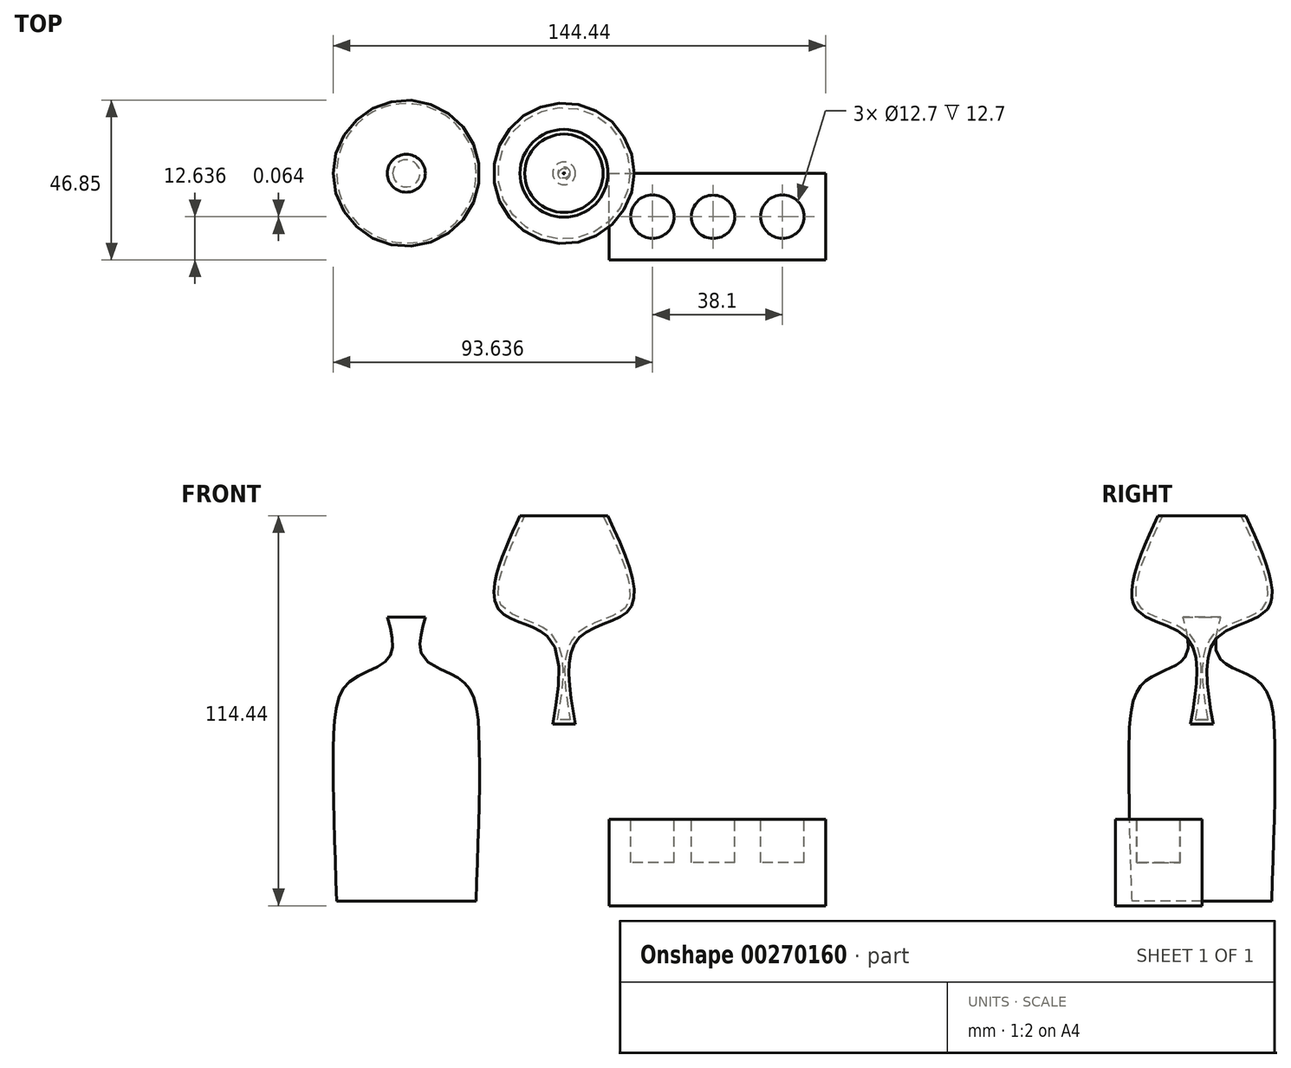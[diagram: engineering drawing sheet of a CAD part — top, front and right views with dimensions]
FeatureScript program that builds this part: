
annotation { "Feature Type Name" : "Feature", "Feature Type Description" : "" }
export const myFeature = defineFeature(function(context is Context, id is Id, definition is map)
    precondition{}
    {
        {
            var Q0;
            Q0=qCreatedBy(makeId("Front.planeOp"),FACE);
            var sketch = newSketch(context, id + "F0", { "sketchPlane" : qUnion([Q0])});
            skFitSpline(sketch, "E0", {"points": [v(12.9, 61.12) * mm, v(19.34, 33.78) * mm, v(4.45, 25.34) * mm, v(3.33, 0) * mm], "startDerivative": vector(41.44, -90.86) * mm, "endDerivative": vector(15.34, -88.17) * mm});
            skLineSegment(sketch, "E1", {"start": v(12.9, 61.12) * mm, "end": v(0, 61.12) * mm});
            skLineSegment(sketch, "E2", {"start": v(0, 0) * mm, "end": v(3.33, 0) * mm});
            skLineSegment(sketch, "E3", {"start": v(0, 61.12) * mm, "end": v(0, 0) * mm});
            skSolve(sketch);
        }
        {
            var Q0;
            Q0=makeQuery(id+"F0.imprint","IMPRINT",FACE,{"disambiguationData":[TD([[makeQuery(id+"F0.imprint","IMPRINT",EDGE,{"derivedFrom":sQuery(id+"F0.wireOp",EDGE,"E0")}),-1.0]])]});
            var Q1;
            Q1=sQuery(id+"F0.wireOp",EDGE,"E3");
            revolve(context, id + "F1", {"entities" : qUnion([Q0]), "axis" : qUnion([Q1]), "revolveType" : RevolveType.FULL});
        }
        {
            var Q0;
            Q0=makeQuery(id+"F1.opRevolve","SWEPT_FACE",FACE,{"disambiguationData":[OSD([sQuery(id+"F0.wireOp",EDGE,"E1")])]});
            shell(context, id + "F2", {"entities" : qUnion([Q0]), "thickness" : 1.27 * mm});
        }
        {
            var Q0;
            Q0=qCreatedBy(makeId("Front.planeOp"),FACE);
            var sketch = newSketch(context, id + "F3", { "sketchPlane" : qUnion([Q0])});
            skFitSpline(sketch, "E4", {"points": [v(-51.78, 31.34) * mm, v(-51.34, 19.34) * mm, v(-62.9, 12.45) * mm, v(-67.56, -4) * mm, v(-66.67, -52) * mm], "startDerivative": vector(19.9, -72.3) * mm, "endDerivative": vector(5.04, -139.57) * mm});
            skFitSpline(sketch, "E5", {"points": [v(-66.67, -52) * mm, v(-46.23, -52) * mm], "startDerivative": vector(20.45, 0) * mm, "endDerivative": vector(20.45, 0) * mm});
            skLineSegment(sketch, "E6", {"start": v(-51.78, 31.34) * mm, "end": v(-38.9, 31.34) * mm});
            skLineSegment(sketch, "E7", {"start": v(-46.23, -52) * mm, "end": v(-46.23, 31.34) * mm});
            skSolve(sketch);
        }
        {
            var Q0;
            {var subQ0=sQuery(id+"F3.wireOp",EDGE,"E4");Q0=makeQuery(id+"F3.imprint","IMPRINT",FACE,{"disambiguationData":[TD([[makeQuery(id+"F3.imprint","IMPRINT",EDGE,{"derivedFrom":subQ0}),1.0]])]});}
            var Q1;
            Q1=sQuery(id+"F3.wireOp",EDGE,"E7");
            revolve(context, id + "F4", {"entities" : qUnion([Q0]), "axis" : qUnion([Q1]), "revolveType" : RevolveType.FULL});
        }
        {
            var Q0;
            Q0=qCreatedBy(makeId("Front.planeOp"),FACE);
            var sketch = newSketch(context, id + "F5", { "sketchPlane" : qUnion([Q0])});
            skLineSegment(sketch, "E8.bottom", {"start": v(13.26, -27.92) * mm, "end": v(76.76, -27.92) * mm});
            skLineSegment(sketch, "E8.top", {"start": v(13.26, -53.32) * mm, "end": v(76.76, -53.32) * mm});
            skLineSegment(sketch, "E8.left", {"start": v(13.26, -27.92) * mm, "end": v(13.26, -53.32) * mm});
            skLineSegment(sketch, "E8.right", {"start": v(76.76, -27.92) * mm, "end": v(76.76, -53.32) * mm});
            skSolve(sketch);
        }
        {
            var Q0;
            Q0 = qSketchRegion(id + "F5", true);
            extrude(context, id + "F6", {"entities" : qUnion([Q0]), "depth" : 25.4 * mm});
        }
        {
            var Q0;
            Q0=makeQuery(id+"F6.opExtrude","SWEPT_FACE",FACE,{"disambiguationData":[OSD([sQuery(id+"F5.wireOp",EDGE,"E8.bottom")])]});
            var sketch = newSketch(context, id + "F7", { "sketchPlane" : qUnion([Q0])});
            skCircle(sketch, "E9", {"center": v(25.96, -12.7) * mm, "radius": 6.35 * mm});
            skCircle(sketch, "E10", {"center": v(43.74, -12.76) * mm, "radius": 6.35 * mm});
            skCircle(sketch, "E11", {"center": v(64.06, -12.7) * mm, "radius": 6.35 * mm});
            skSolve(sketch);
        }
        {
            var Q0;
            Q0 = qSketchRegion(id + "F7", true);
            extrude(context, id + "F8", {"entities" : qUnion([Q0]), "operationType" : NewBodyOperationType.REMOVE, "oppositeDirection" : true, "depth" : 12.7 * mm});
        }
    });
